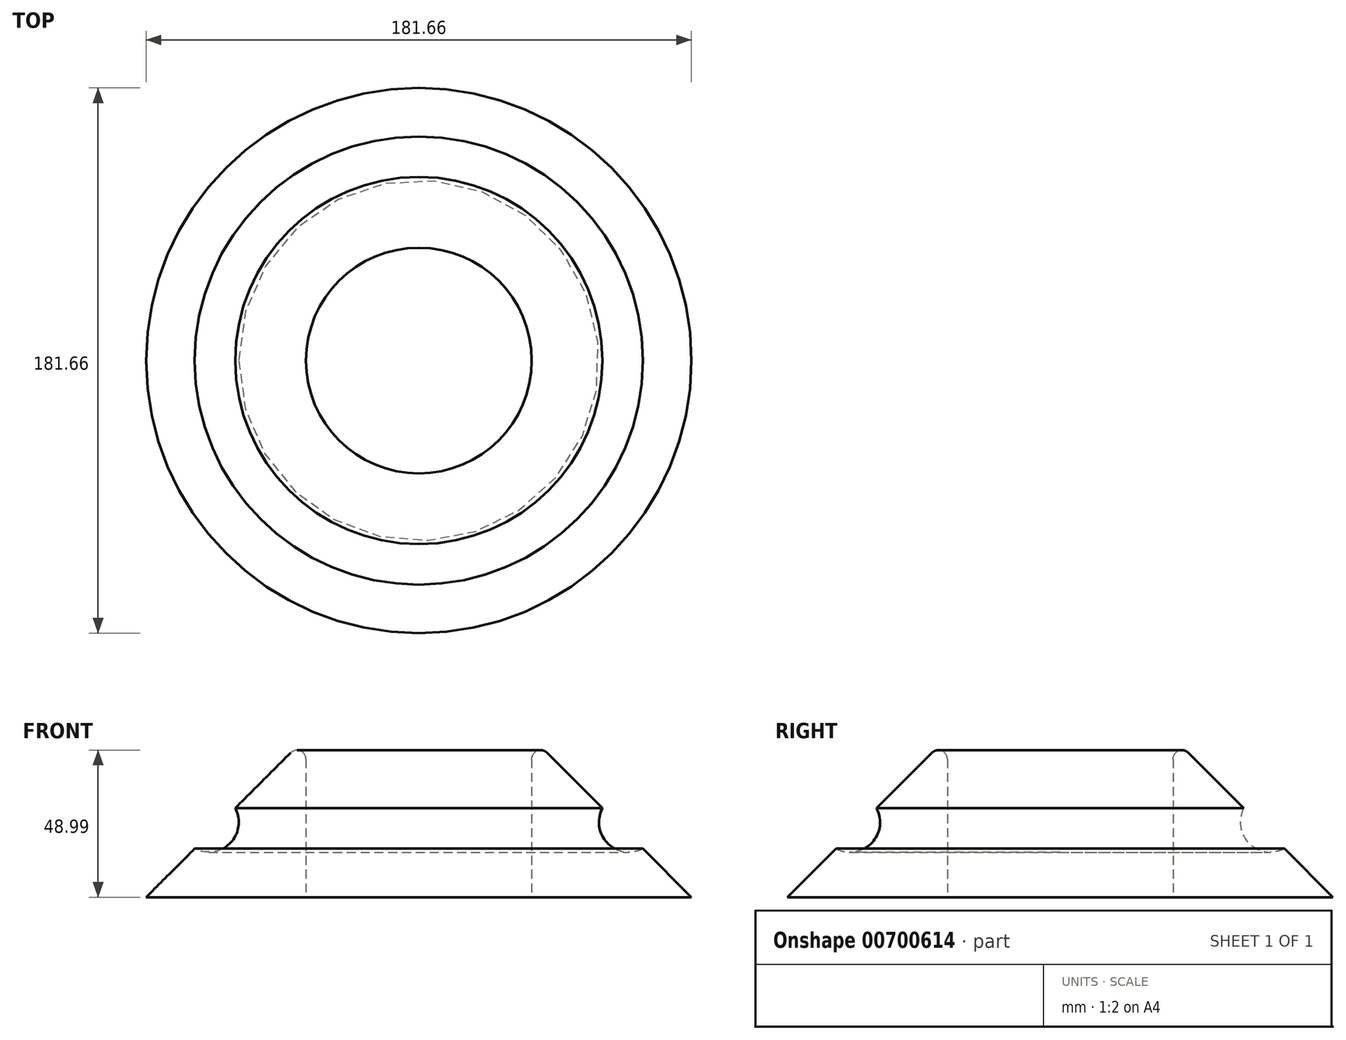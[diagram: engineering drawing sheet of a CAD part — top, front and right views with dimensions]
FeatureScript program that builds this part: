
annotation { "Feature Type Name" : "Feature", "Feature Type Description" : "" }
export const myFeature = defineFeature(function(context is Context, id is Id, definition is map)
    precondition{}
    {
        {
            var Q0;
            Q0=qCreatedBy(makeId("Right.planeOp"),FACE);
            var sketch = newSketch(context, id + "F0", { "sketchPlane" : qUnion([Q0])});
            skLineSegment(sketch, "E0", {"start": v(-37.6, 0) * mm, "end": v(-37.6, 45.99) * mm});
            skLineSegment(sketch, "E1", {"start": v(-42.72, 48.1) * mm, "end": v(-90.83, 0) * mm});
            skLineSegment(sketch, "E2", {"start": v(-90.83, 0) * mm, "end": v(-37.6, 0) * mm});
            skPoint(sketch, "E3.visualSharp", {"position": v(-37.6, 53.23) * mm});
            skArc(sketch, "E3.filletArc", {"start": v(-37.6, 45.99) * mm, "mid": v(-39.45, 48.76) * mm, "end": v(-42.72, 48.1) * mm});
            skLineSegment(sketch, "E4", {"start": v(0, 0) * mm, "end": v(0, 77.44) * mm, "construction": true});
            skSolve(sketch);
        }
        {
            var Q0;
            Q0 = qSketchRegion(id + "F0", true);
            var Q1;
            Q1=sQuery(id+"F0.wireOp",EDGE,"E4");
            revolve(context, id + "F1", {"entities" : qUnion([Q0]), "axis" : qUnion([Q1]), "revolveType" : RevolveType.FULL});
        }
        {
            var Q0;
            Q0=qCreatedBy(makeId("Right.planeOp"),FACE);
            var sketch = newSketch(context, id + "F2", { "sketchPlane" : qUnion([Q0])});
            skCircle(sketch, "E5", {"center": v(-70, 25) * mm, "radius": 10 * mm});
            skLineSegment(sketch, "E6", {"start": v(0, 0) * mm, "end": v(0, 58.37) * mm, "construction": true});
            skSolve(sketch);
        }
        {
            var Q0;
            Q0 = qSketchRegion(id + "F2", true);
            var Q1;
            Q1=sQuery(id+"F2.wireOp",EDGE,"E6");
            revolve(context, id + "F3", {"operationType" : NewBodyOperationType.REMOVE, "entities" : qUnion([Q0]), "axis" : qUnion([Q1]), "revolveType" : RevolveType.FULL, "oppositeDirection" : true});
        }
    });
